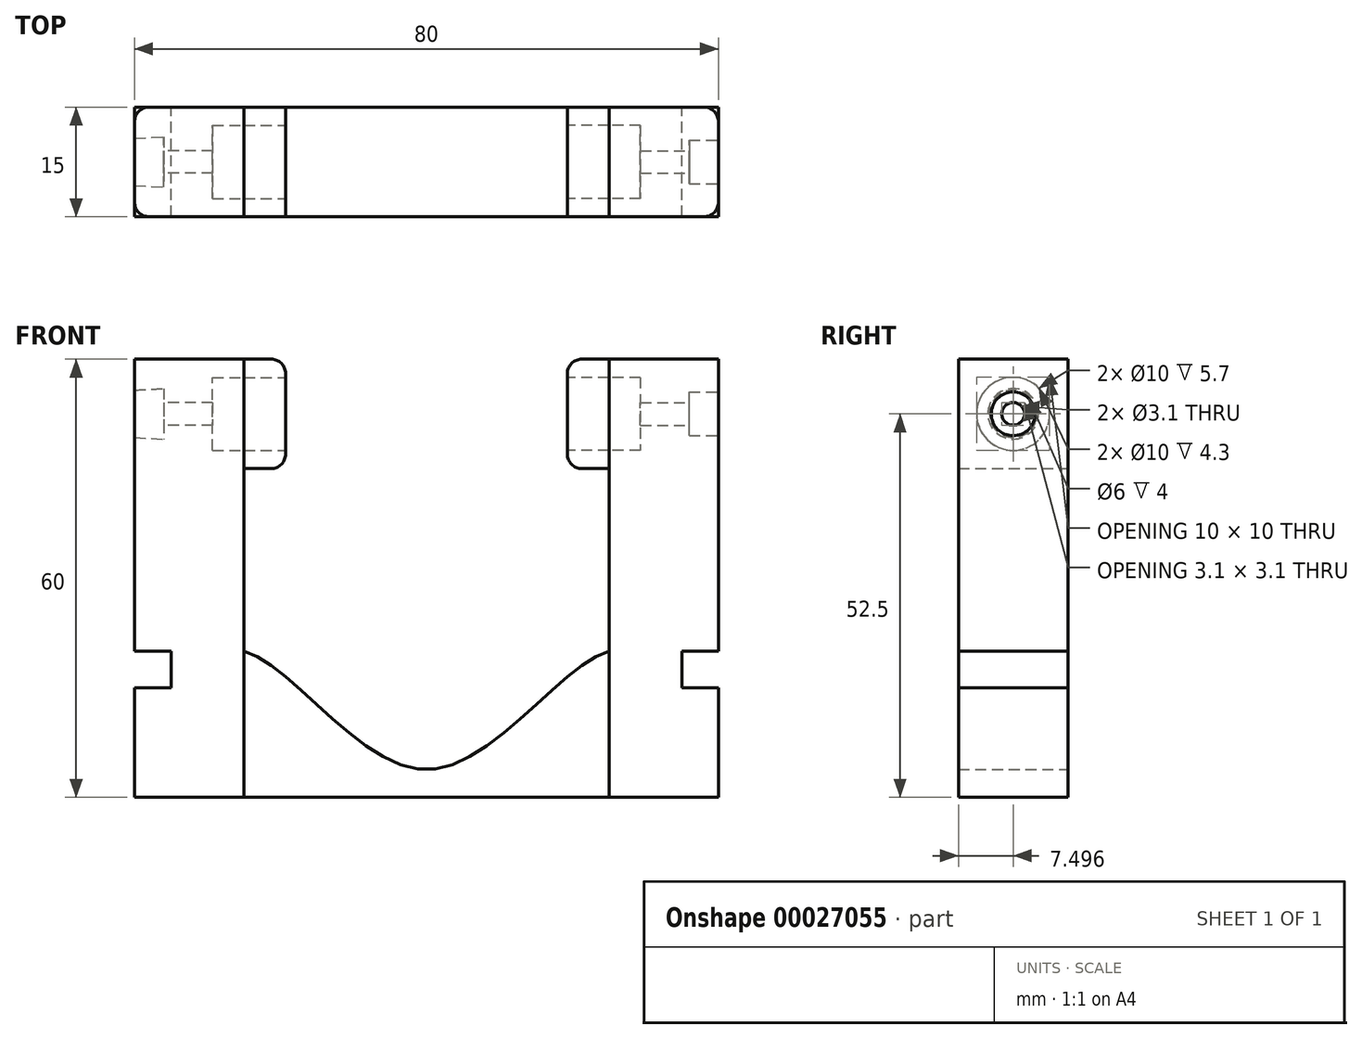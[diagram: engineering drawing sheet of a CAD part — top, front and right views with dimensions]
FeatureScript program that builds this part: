
annotation { "Feature Type Name" : "Feature", "Feature Type Description" : "" }
export const myFeature = defineFeature(function(context is Context, id is Id, definition is map)
    precondition{}
    {
        {
            var Q0;
            Q0=qCreatedBy(makeId("Top.planeOp"),FACE);
            var sketch = newSketch(context, id + "F0", { "sketchPlane" : qUnion([Q0])});
            skLineSegment(sketch, "E0.bottom", {"start": v(-25.06, 38.5) * mm, "end": v(-10.06, 38.5) * mm});
            skLineSegment(sketch, "E0.top", {"start": v(-25.06, 23.5) * mm, "end": v(-10.06, 23.5) * mm});
            skLineSegment(sketch, "E0.left", {"start": v(-25.06, 38.5) * mm, "end": v(-25.06, 23.5) * mm});
            skLineSegment(sketch, "E0.right", {"start": v(-10.06, 38.5) * mm, "end": v(-10.06, 23.5) * mm});
            skLineSegment(sketch, "E1.bottom", {"start": v(39.94, 38.5) * mm, "end": v(54.94, 38.5) * mm});
            skLineSegment(sketch, "E1.top", {"start": v(39.94, 23.5) * mm, "end": v(54.94, 23.5) * mm});
            skLineSegment(sketch, "E1.left", {"start": v(39.94, 38.5) * mm, "end": v(39.94, 23.5) * mm});
            skLineSegment(sketch, "E1.right", {"start": v(54.94, 38.5) * mm, "end": v(54.94, 23.5) * mm});
            skSolve(sketch);
        }
        {
            var Q0;
            Q0=makeQuery(id+"F0.imprint","IMPRINT",FACE,{"disambiguationData":[TD([[makeQuery(id+"F0.imprint","IMPRINT",EDGE,{"derivedFrom":sQuery(id+"F0.wireOp",EDGE,"E0.bottom")}),-1.0]])]});
            var Q1;
            Q1=makeQuery(id+"F0.imprint","IMPRINT",FACE,{"disambiguationData":[TD([[makeQuery(id+"F0.imprint","IMPRINT",EDGE,{"derivedFrom":sQuery(id+"F0.wireOp",EDGE,"E1.bottom")}),-1.0]])]});
            extrude(context, id + "F1", {"entities" : qUnion([Q0, Q1]), "depth" : 60 * mm});
        }
        {
            var Q0;
            Q0=makeQuery(id+"F1.opExtrude","SWEPT_FACE",FACE,{"disambiguationData":[OSD([sQuery(id+"F0.wireOp",EDGE,"E1.bottom")])]});
            var sketch = newSketch(context, id + "F2", { "sketchPlane" : qUnion([Q0])});
            skLineSegment(sketch, "E2.bottom", {"start": v(-39.94, 0) * mm, "end": v(10.06, 0) * mm});
            skLineSegment(sketch, "E2.left", {"start": v(-39.94, 0) * mm, "end": v(-39.94, 20) * mm});
            skLineSegment(sketch, "E2.right", {"start": v(10.06, 0) * mm, "end": v(10.06, 20) * mm});
            skFitSpline(sketch, "E3", {"points": [v(-39.94, 20) * mm, v(-14.94, 3.8) * mm, v(10.06, 20) * mm], "startDerivative": vector(40.2, -10.75) * mm, "endDerivative": vector(40.2, 10.75) * mm});
            skLineSegment(sketch, "E4", {"start": v(-14.94, 0) * mm, "end": v(-14.94, 60.06) * mm, "construction": true});
            skSolve(sketch);
        }
        {
            var Q0;
            Q0=makeQuery(id+"F2.imprint","IMPRINT",FACE,{"disambiguationData":[TD([[makeQuery(id+"F2.imprint","IMPRINT",EDGE,{"derivedFrom":sQuery(id+"F2.wireOp",EDGE,"E2.bottom")}),1.0]])]});
            extrude(context, id + "F3", {"entities" : qUnion([Q0]), "oppositeDirection" : true, "depth" : 15 * mm});
        }
        {
            var Q0;
            Q0=makeQuery(id+"F1.opExtrude","SWEPT_FACE",FACE,{"disambiguationData":[OSD([sQuery(id+"F0.wireOp",EDGE,"E1.bottom")])]});
            var sketch = newSketch(context, id + "F4", { "sketchPlane" : qUnion([Q0])});
            skLineSegment(sketch, "E5.bottom", {"start": v(-39.94, 60) * mm, "end": v(-34.24, 60) * mm});
            skLineSegment(sketch, "E5.top", {"start": v(-39.94, 45) * mm, "end": v(-34.24, 45) * mm});
            skLineSegment(sketch, "E5.left", {"start": v(-39.94, 60) * mm, "end": v(-39.94, 45) * mm});
            skLineSegment(sketch, "E5.right", {"start": v(-34.24, 60) * mm, "end": v(-34.24, 45) * mm});
            skLineSegment(sketch, "E6.bottom", {"start": v(10.06, 60) * mm, "end": v(4.36, 60) * mm});
            skLineSegment(sketch, "E6.top", {"start": v(10.06, 45) * mm, "end": v(4.36, 45) * mm});
            skLineSegment(sketch, "E6.left", {"start": v(10.06, 60) * mm, "end": v(10.06, 45) * mm});
            skLineSegment(sketch, "E6.right", {"start": v(4.36, 60) * mm, "end": v(4.36, 45) * mm});
            skSolve(sketch);
        }
        {
            var Q0;
            Q0=makeQuery(id+"F4.imprint","IMPRINT",FACE,{"disambiguationData":[TD([[makeQuery(id+"F4.imprint","IMPRINT",EDGE,{"derivedFrom":sQuery(id+"F4.wireOp",EDGE,"E6.bottom")}),1.0]])]});
            var Q1;
            Q1=makeQuery(id+"F4.imprint","IMPRINT",FACE,{"disambiguationData":[TD([[makeQuery(id+"F4.imprint","IMPRINT",EDGE,{"derivedFrom":sQuery(id+"F4.wireOp",EDGE,"E5.bottom")}),-1.0]])]});
            extrude(context, id + "F5", {"entities" : qUnion([Q0, Q1]), "oppositeDirection" : true, "depth" : 15 * mm});
        }
        {
            var Q0;
            Q0=makeQuery(id+"F5.opExtrude","SWEPT_FACE",FACE,{"disambiguationData":[OSD([sQuery(id+"F4.wireOp",EDGE,"E6.right")])]});
            var sketch = newSketch(context, id + "F6", { "sketchPlane" : qUnion([Q0])});
            skLineSegment(sketch, "E7", {"start": v(31, 45) * mm, "end": v(31, 60) * mm, "construction": true});
            skLineSegment(sketch, "E8", {"start": v(38.5, 52.5) * mm, "end": v(23.5, 52.5) * mm, "construction": true});
            skCircle(sketch, "E9", {"center": v(31, 52.5) * mm, "radius": 5 * mm});
            skSolve(sketch);
        }
        {
            var Q0;
            Q0=makeQuery(id+"F6.imprint","IMPRINT",FACE,{"disambiguationData":[TD([[makeQuery(id+"F6.imprint","IMPRINT",EDGE,{"derivedFrom":sQuery(id+"F6.wireOp",EDGE,"E9")}),1.0]])]});
            extrude(context, id + "F7", {"entities" : qUnion([Q0]), "operationType" : NewBodyOperationType.REMOVE, "oppositeDirection" : true, "depth" : 10 * mm});
        }
        {
            var Q0;
            Q0=makeQuery(id+"F5.opExtrude","SWEPT_FACE",FACE,{"disambiguationData":[OSD([sQuery(id+"F4.wireOp",EDGE,"E5.right")])]});
            var sketch = newSketch(context, id + "F8", { "sketchPlane" : qUnion([Q0])});
            skLineSegment(sketch, "E10", {"start": v(-31, 45) * mm, "end": v(-31, 60) * mm, "construction": true});
            skLineSegment(sketch, "E11", {"start": v(-23.5, 52.5) * mm, "end": v(-38.5, 52.5) * mm, "construction": true});
            skCircle(sketch, "E12", {"center": v(-31, 52.5) * mm, "radius": 5 * mm});
            skSolve(sketch);
        }
        {
            var Q0;
            Q0=makeQuery(id+"F8.imprint","IMPRINT",FACE,{"disambiguationData":[TD([[makeQuery(id+"F8.imprint","IMPRINT",EDGE,{"derivedFrom":sQuery(id+"F8.wireOp",EDGE,"E12")}),1.0]])]});
            extrude(context, id + "F9", {"entities" : qUnion([Q0]), "operationType" : NewBodyOperationType.REMOVE, "oppositeDirection" : true, "depth" : 10 * mm});
        }
        {
            var Q0;
            Q0=makeQuery(id+"F1.opExtrude","SWEPT_FACE",FACE,{"disambiguationData":[OSD([sQuery(id+"F0.wireOp",EDGE,"E0.left")])]});
            var sketch = newSketch(context, id + "F10", { "sketchPlane" : qUnion([Q0])});
            skLineSegment(sketch, "E13", {"start": v(-23.5, 45) * mm, "end": v(-38.5, 45) * mm});
            skLineSegment(sketch, "E14", {"start": v(-31, 45) * mm, "end": v(-31, 60) * mm, "construction": true});
            skLineSegment(sketch, "E15", {"start": v(-23.5, 52.5) * mm, "end": v(-38.5, 52.5) * mm, "construction": true});
            skCircle(sketch, "E16", {"center": v(-31, 52.5) * mm, "radius": 3.25 * mm});
            skCircle(sketch, "E17", {"center": v(-31, 52.5) * mm, "radius": 1.55 * mm});
            skSolve(sketch);
        }
        {
            var Q0;
            Q0=makeQuery(id+"F10.imprint","IMPRINT",FACE,{"disambiguationData":[TD([[makeQuery(id+"F10.imprint","IMPRINT",EDGE,{"derivedFrom":sQuery(id+"F10.wireOp",EDGE,"E17")}),1.0]])]});
            extrude(context, id + "F11", {"entities" : qUnion([Q0]), "operationType" : NewBodyOperationType.REMOVE, "oppositeDirection" : true, "depth" : 25 * mm});
        }
        {
            var Q0;
            Q0=makeQuery(id+"F10.imprint","IMPRINT",FACE,{"disambiguationData":[TD([[makeQuery(id+"F10.imprint","IMPRINT",EDGE,{"derivedFrom":sQuery(id+"F10.wireOp",EDGE,"E16")}),1.0]])]});
            extrude(context, id + "F12", {"entities" : qUnion([Q0]), "operationType" : NewBodyOperationType.REMOVE, "oppositeDirection" : true, "depth" : 4 * mm, "hasDraft" : true, "draftAngle" : 3 * degree});
        }
        {
            var Q0;
            Q0=makeQuery(id+"F1.opExtrude","SWEPT_FACE",FACE,{"disambiguationData":[OSD([sQuery(id+"F0.wireOp",EDGE,"E1.right")])]});
            var sketch = newSketch(context, id + "F13", { "sketchPlane" : qUnion([Q0])});
            skLineSegment(sketch, "E18", {"start": v(38.5, 45) * mm, "end": v(23.5, 45) * mm, "construction": true});
            skLineSegment(sketch, "E19", {"start": v(31, 45) * mm, "end": v(31, 60) * mm, "construction": true});
            skLineSegment(sketch, "E20", {"start": v(38.5, 52.5) * mm, "end": v(23.5, 52.5) * mm, "construction": true});
            skPoint(sketch, "E21.center.orphan", {"position": v(31, 52.5) * mm});
            skCircle(sketch, "E22", {"center": v(31, 52.5) * mm, "radius": 1.55 * mm});
            skCircle(sketch, "E23", {"center": v(31, 52.5) * mm, "radius": 3 * mm});
            skSolve(sketch);
        }
        {
            var Q0;
            Q0=makeQuery(id+"F13.imprint","IMPRINT",FACE,{"disambiguationData":[TD([[makeQuery(id+"F13.imprint","IMPRINT",EDGE,{"derivedFrom":sQuery(id+"F13.wireOp",EDGE,"E22")}),1.0]])]});
            extrude(context, id + "F14", {"entities" : qUnion([Q0]), "operationType" : NewBodyOperationType.REMOVE, "oppositeDirection" : true, "depth" : 25 * mm});
        }
        {
            var Q0;
            Q0=makeQuery(id+"F13.imprint","IMPRINT",FACE,{"disambiguationData":[TD([[makeQuery(id+"F13.imprint","IMPRINT",EDGE,{"derivedFrom":sQuery(id+"F13.wireOp",EDGE,"E22")}),-1.0]])]});
            extrude(context, id + "F15", {"entities" : qUnion([Q0]), "operationType" : NewBodyOperationType.REMOVE, "oppositeDirection" : true, "depth" : 4 * mm});
        }
        {
            var Q0;
            Q0=makeQuery(id+"F1.opExtrude","SWEPT_FACE",FACE,{"disambiguationData":[OSD([sQuery(id+"F0.wireOp",EDGE,"E0.bottom")])]});
            var sketch = newSketch(context, id + "F16", { "sketchPlane" : qUnion([Q0])});
            skLineSegment(sketch, "E24.bottom", {"start": v(25.06, 15) * mm, "end": v(20.06, 15) * mm});
            skLineSegment(sketch, "E24.top", {"start": v(25.06, 20) * mm, "end": v(20.06, 20) * mm});
            skLineSegment(sketch, "E24.right", {"start": v(20.06, 15) * mm, "end": v(20.06, 20) * mm});
            skSolve(sketch);
        }
        {
            var Q0;
            {var subQ2=sQuery(id+"F16.wireOp",EDGE,"E24.bottom");Q0=makeQuery(id+"F16.imprint","IMPRINT",FACE,{"disambiguationData":[TD([[makeQuery(id+"F16.imprint","IMPRINT",EDGE,{"derivedFrom":subQ2}),-1.0]])]});}
            extrude(context, id + "F17", {"entities" : qUnion([Q0]), "operationType" : NewBodyOperationType.REMOVE, "oppositeDirection" : true, "depth" : 25 * mm});
        }
        {
            var Q0;
            Q0=makeQuery(id+"F1.opExtrude","SWEPT_FACE",FACE,{"disambiguationData":[OSD([sQuery(id+"F0.wireOp",EDGE,"E1.bottom")])]});
            var sketch = newSketch(context, id + "F18", { "sketchPlane" : qUnion([Q0])});
            skLineSegment(sketch, "E25.bottom", {"start": v(-54.94, 15) * mm, "end": v(-49.94, 15) * mm});
            skLineSegment(sketch, "E25.top", {"start": v(-54.94, 20) * mm, "end": v(-49.94, 20) * mm});
            skLineSegment(sketch, "E25.right", {"start": v(-49.94, 15) * mm, "end": v(-49.94, 20) * mm});
            skSolve(sketch);
        }
        {
            var Q0;
            {var subQ2=sQuery(id+"F18.wireOp",EDGE,"E25.bottom");Q0=makeQuery(id+"F18.imprint","IMPRINT",FACE,{"disambiguationData":[TD([[makeQuery(id+"F18.imprint","IMPRINT",EDGE,{"derivedFrom":subQ2}),1.0]])]});}
            extrude(context, id + "F19", {"entities" : qUnion([Q0]), "operationType" : NewBodyOperationType.REMOVE, "oppositeDirection" : true, "depth" : 25 * mm});
        }
        {
            var Q0;
            Q0=makeQuery(id+"F5.opExtrude","SWEPT_EDGE",EDGE,{"disambiguationData":[OSD([sQuery(id+"F4.wireOp",EDGE,"E6.top"),sQuery(id+"F4.wireOp",EDGE,"E6.right")])]});
            var Q1;
            Q1=makeQuery(id+"F5.opExtrude","SWEPT_EDGE",EDGE,{"disambiguationData":[OSD([sQuery(id+"F4.wireOp",EDGE,"E6.bottom"),sQuery(id+"F4.wireOp",EDGE,"E6.right")])]});
            var Q2;
            Q2=makeQuery(id+"F5.opExtrude","SWEPT_EDGE",EDGE,{"disambiguationData":[OSD([sQuery(id+"F4.wireOp",EDGE,"E5.bottom"),sQuery(id+"F4.wireOp",EDGE,"E5.right")])]});
            var Q3;
            Q3=makeQuery(id+"F5.opExtrude","SWEPT_EDGE",EDGE,{"disambiguationData":[OSD([sQuery(id+"F4.wireOp",EDGE,"E5.top"),sQuery(id+"F4.wireOp",EDGE,"E5.right")])]});
            var Q4;
            {var subQ0=sQuery(id+"F0.wireOp",EDGE,"E0.bottom");var subQ1=sQuery(id+"F0.wireOp",EDGE,"E0.left");Q4=makeQuery(id+"F17.boolean.opBoolean","SPLIT",EDGE,{"disambiguationData":[TD([makeQuery(id+"F17.opExtrude","SWEPT_FACE",FACE,{"disambiguationData":[OSD([sQuery(id+"F16.wireOp",EDGE,"E24.top")])]})])],"derivedFrom":makeQuery(id+"F1.opExtrude","SWEPT_EDGE",EDGE,{"disambiguationData":[OSD([subQ0,subQ1])]})});}
            var Q5;
            {var subQ0=sQuery(id+"F0.wireOp",EDGE,"E0.top");var subQ1=sQuery(id+"F0.wireOp",EDGE,"E0.left");Q5=makeQuery(id+"F17.boolean.opBoolean","SPLIT",EDGE,{"disambiguationData":[TD([makeQuery(id+"F17.opExtrude","SWEPT_FACE",FACE,{"disambiguationData":[OSD([sQuery(id+"F16.wireOp",EDGE,"E24.top")])]})])],"derivedFrom":makeQuery(id+"F1.opExtrude","SWEPT_EDGE",EDGE,{"disambiguationData":[OSD([subQ0,subQ1])]})});}
            var Q6;
            {var subQ0=sQuery(id+"F0.wireOp",EDGE,"E1.bottom");var subQ1=sQuery(id+"F0.wireOp",EDGE,"E1.right");Q6=makeQuery(id+"F19.boolean.opBoolean","SPLIT",EDGE,{"disambiguationData":[TD([makeQuery(id+"F19.opExtrude","SWEPT_FACE",FACE,{"disambiguationData":[OSD([sQuery(id+"F18.wireOp",EDGE,"E25.top")])]})])],"derivedFrom":makeQuery(id+"F1.opExtrude","SWEPT_EDGE",EDGE,{"disambiguationData":[OSD([subQ0,subQ1])]})});}
            var Q7;
            {var subQ0=sQuery(id+"F0.wireOp",EDGE,"E1.top");var subQ1=sQuery(id+"F0.wireOp",EDGE,"E1.right");Q7=makeQuery(id+"F19.boolean.opBoolean","SPLIT",EDGE,{"disambiguationData":[TD([makeQuery(id+"F19.opExtrude","SWEPT_FACE",FACE,{"disambiguationData":[OSD([sQuery(id+"F18.wireOp",EDGE,"E25.top")])]})])],"derivedFrom":makeQuery(id+"F1.opExtrude","SWEPT_EDGE",EDGE,{"disambiguationData":[OSD([subQ0,subQ1])]})});}
            fillet(context, id + "F20", {"entities" : qUnion([Q0, Q1, Q2, Q3, Q4, Q5, Q6, Q7]), "radius" : 2 * mm, "tangentPropagation" : true, "allowEdgeOverflow" : false});
        }
    });
